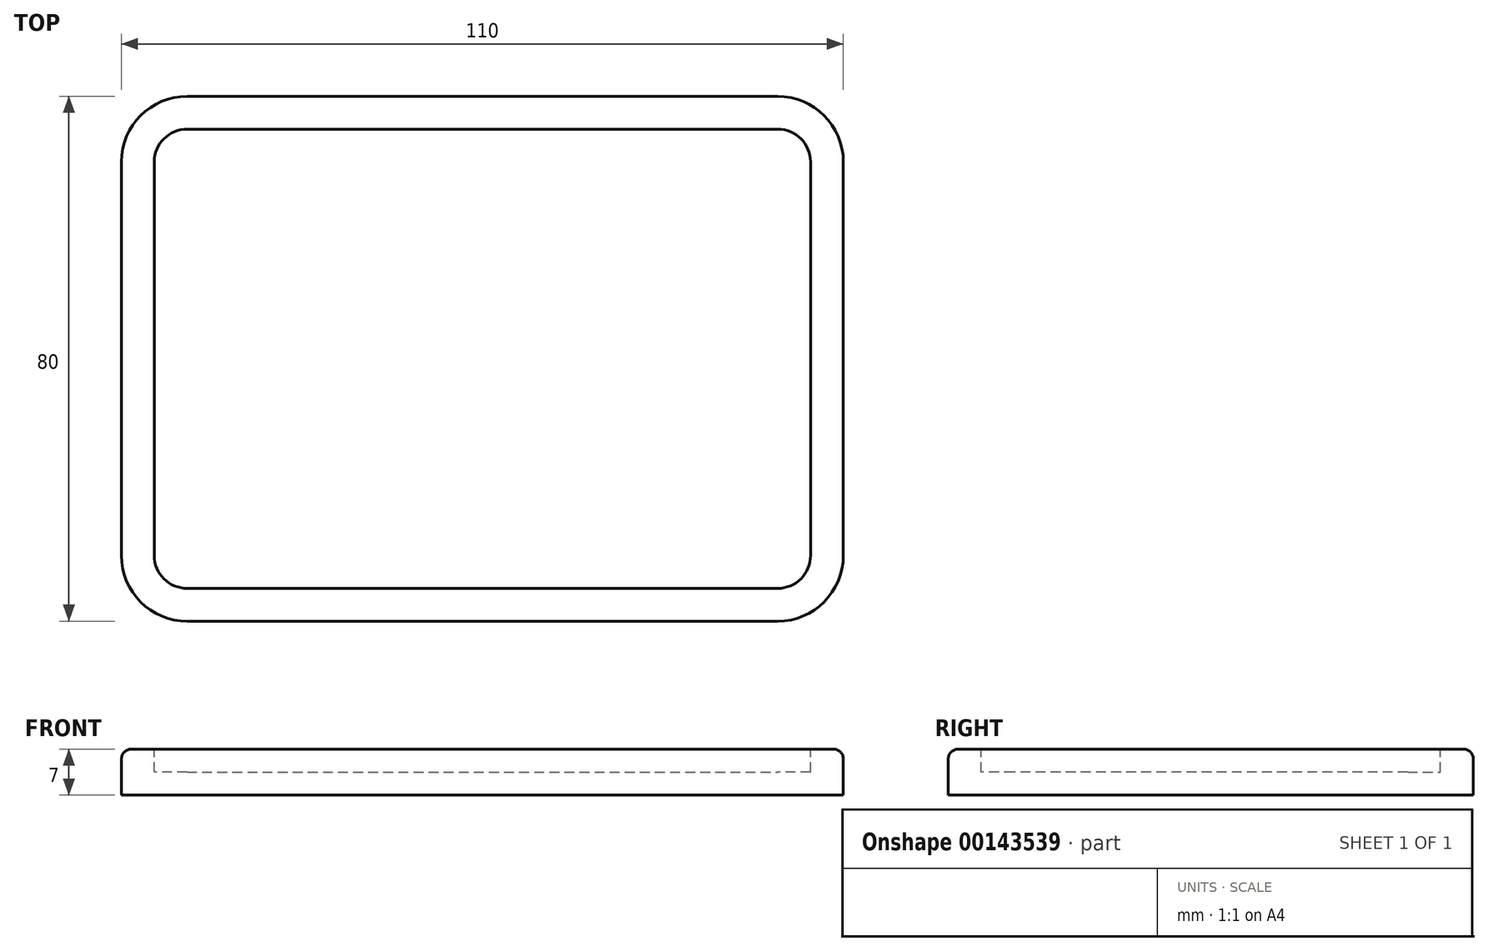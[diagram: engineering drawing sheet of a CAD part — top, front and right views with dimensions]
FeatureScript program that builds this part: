
annotation { "Feature Type Name" : "Feature", "Feature Type Description" : "" }
export const myFeature = defineFeature(function(context is Context, id is Id, definition is map)
    precondition{}
    {
        {
            var Q0;
            Q0=qCreatedBy(makeId("Top.planeOp"),FACE);
            var sketch = newSketch(context, id + "F0", { "sketchPlane" : qUnion([Q0])});
            skLineSegment(sketch, "E0.bottom", {"start": v(-55, 40) * mm, "end": v(55, 40) * mm});
            skLineSegment(sketch, "E0.top", {"start": v(-55, -40) * mm, "end": v(55, -40) * mm});
            skLineSegment(sketch, "E0.left", {"start": v(-55, 40) * mm, "end": v(-55, -40) * mm});
            skLineSegment(sketch, "E0.right", {"start": v(55, 40) * mm, "end": v(55, -40) * mm});
            skSolve(sketch);
        }
        {
            var Q0;
            Q0=makeQuery(id+"F0.imprint","IMPRINT",FACE,{"disambiguationData":[TD([[makeQuery(id+"F0.imprint","IMPRINT",EDGE,{"derivedFrom":sQuery(id+"F0.wireOp",EDGE,"E0.bottom")}),-1.0]])]});
            extrude(context, id + "F1", {"entities" : qUnion([Q0]), "depth" : 7 * mm});
        }
        {
            var Q0;
            Q0=makeQuery(id+"F1.opExtrude","CAP_FACE",FACE,{"disambiguationData":[OSD([sQuery(id+"F0.wireOp",EDGE,"E0.bottom"),sQuery(id+"F0.wireOp",EDGE,"E0.top"),sQuery(id+"F0.wireOp",EDGE,"E0.left"),sQuery(id+"F0.wireOp",EDGE,"E0.right")])],"isStart":false});
            var sketch = newSketch(context, id + "F2", { "sketchPlane" : qUnion([Q0])});
            skLineSegment(sketch, "E1.0", {"start": v(-50, 35) * mm, "end": v(-50, -35) * mm});
            skLineSegment(sketch, "E1.1", {"start": v(-50, 35) * mm, "end": v(50, 35) * mm});
            skLineSegment(sketch, "E1.2", {"start": v(50, 35) * mm, "end": v(50, -35) * mm});
            skLineSegment(sketch, "E1.3", {"start": v(-50, -35) * mm, "end": v(50, -35) * mm});
            skSolve(sketch);
        }
        {
            var Q0;
            Q0=makeQuery(id+"F2.imprint","IMPRINT",FACE,{"disambiguationData":[TD([[makeQuery(id+"F2.imprint","IMPRINT",EDGE,{"derivedFrom":sQuery(id+"F2.wireOp",EDGE,"E1.0")}),1.0]])]});
            extrude(context, id + "F3", {"entities" : qUnion([Q0]), "operationType" : NewBodyOperationType.REMOVE, "oppositeDirection" : true, "depth" : 3.5 * mm});
        }
        {
            var Q0;
            Q0=makeQuery(id+"F3.boolean.opBoolean","COPY",EDGE,{"derivedFrom":makeQuery(id+"F3.opExtrude","SWEPT_EDGE",EDGE,{"disambiguationData":[OSD([sQuery(id+"F2.wireOp",EDGE,"E1.2"),sQuery(id+"F2.wireOp",EDGE,"E1.3")])]})});
            var Q1;
            Q1=makeQuery(id+"F3.boolean.opBoolean","COPY",EDGE,{"derivedFrom":makeQuery(id+"F3.opExtrude","SWEPT_EDGE",EDGE,{"disambiguationData":[OSD([sQuery(id+"F2.wireOp",EDGE,"E1.0"),sQuery(id+"F2.wireOp",EDGE,"E1.3")])]})});
            var Q2;
            Q2=makeQuery(id+"F3.boolean.opBoolean","COPY",EDGE,{"derivedFrom":makeQuery(id+"F3.opExtrude","SWEPT_EDGE",EDGE,{"disambiguationData":[OSD([sQuery(id+"F2.wireOp",EDGE,"E1.0"),sQuery(id+"F2.wireOp",EDGE,"E1.1")])]})});
            var Q3;
            Q3=makeQuery(id+"F3.boolean.opBoolean","COPY",EDGE,{"derivedFrom":makeQuery(id+"F3.opExtrude","SWEPT_EDGE",EDGE,{"disambiguationData":[OSD([sQuery(id+"F2.wireOp",EDGE,"E1.1"),sQuery(id+"F2.wireOp",EDGE,"E1.2")])]})});
            fillet(context, id + "F4", {"entities" : qUnion([Q0, Q1, Q2, Q3]), "radius" : 5 * mm, "tangentPropagation" : true, "allowEdgeOverflow" : false});
        }
        {
            var Q0;
            Q0=makeQuery(id+"F1.opExtrude","SWEPT_EDGE",EDGE,{"disambiguationData":[OSD([sQuery(id+"F0.wireOp",EDGE,"E0.top"),sQuery(id+"F0.wireOp",EDGE,"E0.left")])]});
            var Q1;
            Q1=makeQuery(id+"F1.opExtrude","SWEPT_EDGE",EDGE,{"disambiguationData":[OSD([sQuery(id+"F0.wireOp",EDGE,"E0.top"),sQuery(id+"F0.wireOp",EDGE,"E0.right")])]});
            var Q2;
            Q2=makeQuery(id+"F1.opExtrude","SWEPT_EDGE",EDGE,{"disambiguationData":[OSD([sQuery(id+"F0.wireOp",EDGE,"E0.bottom"),sQuery(id+"F0.wireOp",EDGE,"E0.right")])]});
            var Q3;
            Q3=makeQuery(id+"F1.opExtrude","SWEPT_EDGE",EDGE,{"disambiguationData":[OSD([sQuery(id+"F0.wireOp",EDGE,"E0.bottom"),sQuery(id+"F0.wireOp",EDGE,"E0.left")])]});
            fillet(context, id + "F5", {"entities" : qUnion([Q0, Q1, Q2, Q3]), "radius" : 10 * mm, "tangentPropagation" : true, "allowEdgeOverflow" : false});
        }
        {
            var Q0;
            Q0=makeQuery(id+"F1.opExtrude","CAP_EDGE",EDGE,{"disambiguationData":[OSD([sQuery(id+"F0.wireOp",EDGE,"E0.top")])],"isStart":false});
            var Q1;
            Q1=makeQuery(id+"F3.boolean.opBoolean","COPY",EDGE,{"derivedFrom":makeQuery(id+"F3.opExtrude","CAP_EDGE",EDGE,{"disambiguationData":[OSD([sQuery(id+"F2.wireOp",EDGE,"E1.2")])],"isStart":true})});
            fillet(context, id + "F6", {"entities" : qUnion([Q0, Q1]), "radius" : 1.5 * mm, "tangentPropagation" : true, "allowEdgeOverflow" : false});
        }
    });
